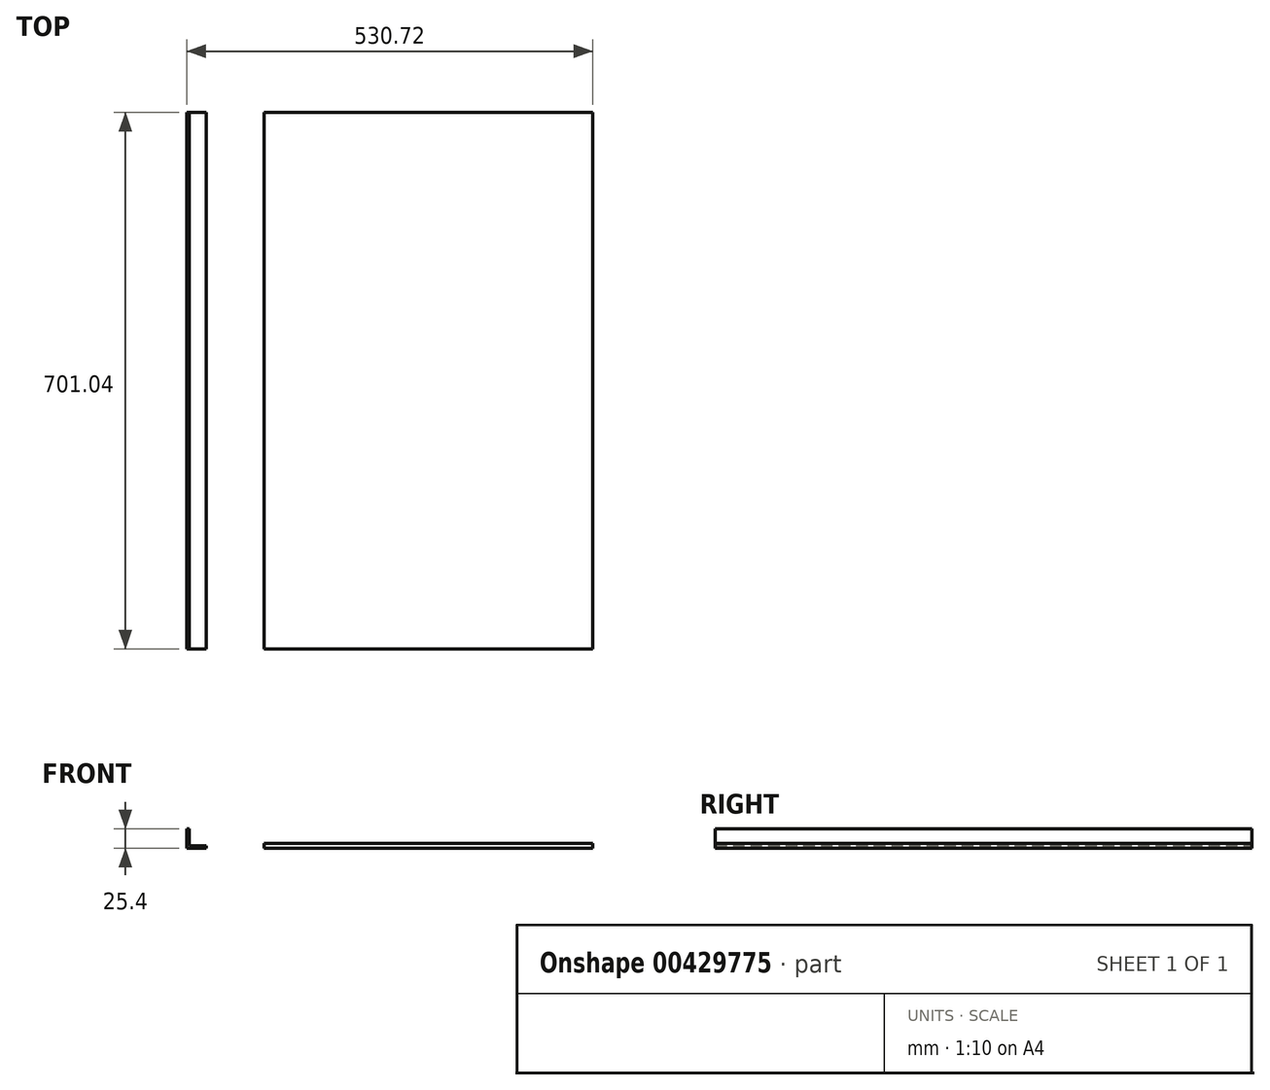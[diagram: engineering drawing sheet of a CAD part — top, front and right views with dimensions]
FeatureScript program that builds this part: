
annotation { "Feature Type Name" : "Feature", "Feature Type Description" : "" }
export const myFeature = defineFeature(function(context is Context, id is Id, definition is map)
    precondition{}
    {
        {
            var Q0;
            Q0=qCreatedBy(makeId("Top.planeOp"),FACE);
            var sketch = newSketch(context, id + "F0", { "sketchPlane" : qUnion([Q0])});
            skLineSegment(sketch, "E0.bottom", {"start": v(0, 0) * mm, "end": v(429.26, 0) * mm});
            skLineSegment(sketch, "E0.right", {"start": v(429.26, 0) * mm, "end": v(429.26, -701.04) * mm});
            skLineSegment(sketch, "E1", {"start": v(0, 0) * mm, "end": v(0, -701.04) * mm});
            skLineSegment(sketch, "E2", {"start": v(0, -701.04) * mm, "end": v(429.26, -701.04) * mm});
            skSolve(sketch);
        }
        {
            var Q0;
            Q0=makeQuery(id+"F0.imprint","IMPRINT",FACE,{"disambiguationData":[TD([[makeQuery(id+"F0.imprint","IMPRINT",EDGE,{"derivedFrom":sQuery(id+"F0.wireOp",EDGE,"E0.bottom")}),-1.0]])]});
            extrude(context, id + "F1", {"entities" : qUnion([Q0]), "depth" : 6.35 * mm});
        }
        {
            var Q0;
            Q0=qCreatedBy(makeId("Front.planeOp"),FACE);
            var sketch = newSketch(context, id + "F2", { "sketchPlane" : qUnion([Q0])});
            skLineSegment(sketch, "E3", {"start": v(-101.46, 0) * mm, "end": v(-101.46, 25.4) * mm});
            skLineSegment(sketch, "E4", {"start": v(-101.46, 25.4) * mm, "end": v(-98.28, 25.4) * mm});
            skLineSegment(sketch, "E5", {"start": v(-101.46, 0) * mm, "end": v(-76.06, 0) * mm});
            skLineSegment(sketch, "E6", {"start": v(-76.06, 0) * mm, "end": v(-76.06, 3.18) * mm});
            skLineSegment(sketch, "E7", {"start": v(-76.06, 3.18) * mm, "end": v(-98.28, 3.18) * mm});
            skLineSegment(sketch, "E8", {"start": v(-98.28, 3.18) * mm, "end": v(-98.28, 25.4) * mm});
            skSolve(sketch);
        }
        {
            var Q0;
            Q0 = qSketchRegion(id + "F2", true);
            extrude(context, id + "F3", {"entities" : qUnion([Q0]), "depth" : 701.04 * mm});
        }
        {
            var Q0;
            Q0=qCreatedBy(makeId("Front.planeOp"),FACE);
            var sketch = newSketch(context, id + "F4", { "sketchPlane" : qUnion([Q0])});
            skLineSegment(sketch, "E9", {"start": v(-66.63, 48.76) * mm, "end": v(-66.63, 74.16) * mm});
            skLineSegment(sketch, "E10", {"start": v(-66.63, 74.16) * mm, "end": v(-63.46, 74.16) * mm});
            skLineSegment(sketch, "E11", {"start": v(-66.63, 48.76) * mm, "end": v(-41.23, 48.76) * mm});
            skLineSegment(sketch, "E12", {"start": v(-41.23, 48.76) * mm, "end": v(-41.23, 51.94) * mm});
            skLineSegment(sketch, "E13", {"start": v(-41.23, 51.94) * mm, "end": v(-63.46, 51.94) * mm});
            skLineSegment(sketch, "E14", {"start": v(-63.46, 51.94) * mm, "end": v(-63.46, 74.16) * mm});
            skSolve(sketch);
        }
        {
            var Q0;
            Q0 = qConstructionFilter(qBodyType(qCreatedBy(id + "F4" ,EDGE), BodyType.WIRE), ConstructionObject.NO);
            extrude(context, id + "F5", {"bodyType" : ToolBodyType.SURFACE, "surfaceEntities" : qUnion([Q0]), "depth" : 429.26 * mm});
        }
        {
            var Q0;
            Q0=qCreatedBy(makeId("Top.planeOp"),FACE);
            var sketch = newSketch(context, id + "F6", { "sketchPlane" : qUnion([Q0])});
            skLineSegment(sketch, "E15", {"start": v(-271.87, -2.66) * mm, "end": v(-271.87, 22.74) * mm});
            skLineSegment(sketch, "E16", {"start": v(-271.87, 22.74) * mm, "end": v(-268.7, 22.74) * mm});
            skLineSegment(sketch, "E17", {"start": v(-271.87, -2.66) * mm, "end": v(-246.47, -2.66) * mm});
            skLineSegment(sketch, "E18", {"start": v(-246.47, -2.66) * mm, "end": v(-246.47, 0.51) * mm});
            skLineSegment(sketch, "E19", {"start": v(-246.47, 0.51) * mm, "end": v(-268.7, 0.51) * mm});
            skLineSegment(sketch, "E20", {"start": v(-268.7, 0.51) * mm, "end": v(-268.7, 22.74) * mm});
            skSolve(sketch);
        }
        {
            var Q0;
            Q0 = qConstructionFilter(qBodyType(qCreatedBy(id + "F6" ,EDGE), BodyType.WIRE), ConstructionObject.NO);
            extrude(context, id + "F7", {"bodyType" : ToolBodyType.SURFACE, "surfaceEntities" : qUnion([Q0]), "depth" : 175.26 * mm});
        }
    });
